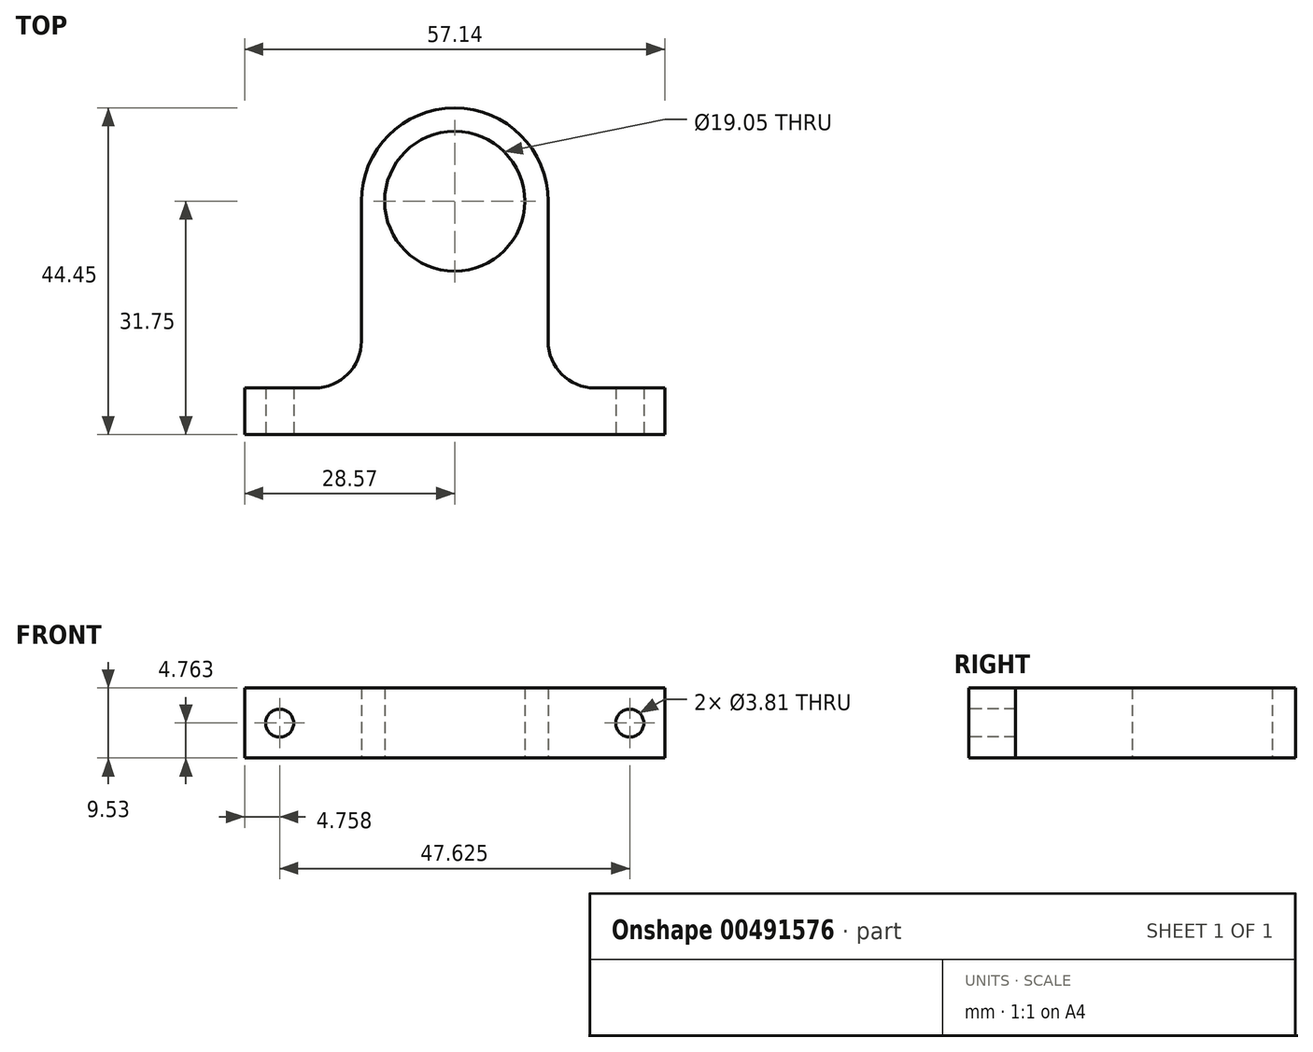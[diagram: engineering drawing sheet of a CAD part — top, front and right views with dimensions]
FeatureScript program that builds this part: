
annotation { "Feature Type Name" : "Feature", "Feature Type Description" : "" }
export const myFeature = defineFeature(function(context is Context, id is Id, definition is map)
    precondition{}
    {
        {
            var Q0;
            Q0=qCreatedBy(makeId("Top.planeOp"),FACE);
            var sketch = newSketch(context, id + "F0", { "sketchPlane" : qUnion([Q0])});
            skLineSegment(sketch, "E0", {"start": v(-28.58, -19.05) * mm, "end": v(-28.58, -12.7) * mm});
            skLineSegment(sketch, "E1", {"start": v(-28.58, -12.7) * mm, "end": v(-19.05, -12.7) * mm});
            skArc(sketch, "E2", {"start": v(-12.7, 12.7) * mm, "mid": v(-8.98, 21.68) * mm, "end": v(0, 25.4) * mm});
            skLineSegment(sketch, "E3", {"start": v(-28.58, -19.05) * mm, "end": v(0, -19.05) * mm});
            skArc(sketch, "E4.MirrorCS", {"start": v(12.7, 12.7) * mm, "mid": v(8.98, 21.68) * mm, "end": v(0, 25.4) * mm});
            skLineSegment(sketch, "E5.MirrorCS", {"start": v(28.58, -12.7) * mm, "end": v(19.05, -12.7) * mm});
            skLineSegment(sketch, "E6.MirrorCS", {"start": v(28.58, -19.05) * mm, "end": v(28.58, -12.7) * mm});
            skLineSegment(sketch, "E7.MirrorCS", {"start": v(28.58, -19.05) * mm, "end": v(0, -19.05) * mm});
            skLineSegment(sketch, "E8", {"start": v(-12.7, 12.7) * mm, "end": v(-12.7, -6.35) * mm});
            skLineSegment(sketch, "E9.MirrorCS", {"start": v(12.7, 12.7) * mm, "end": v(12.7, -6.35) * mm});
            skArc(sketch, "E10", {"start": v(-19.05, -12.7) * mm, "mid": v(-14.56, -10.84) * mm, "end": v(-12.7, -6.35) * mm});
            skArc(sketch, "E11", {"start": v(19.05, -12.7) * mm, "mid": v(14.56, -10.84) * mm, "end": v(12.7, -6.35) * mm});
            skCircle(sketch, "E12", {"center": v(0, 12.7) * mm, "radius": 9.53 * mm});
            skSolve(sketch);
        }
        {
            var Q0;
            Q0=makeQuery(id+"F0.imprint","IMPRINT",FACE,{"disambiguationData":[TD([[makeQuery(id+"F0.imprint","IMPRINT",EDGE,{"derivedFrom":sQuery(id+"F0.wireOp",EDGE,"E0")}),-1.0]])]});
            extrude(context, id + "F1", {"entities" : qUnion([Q0]), "depth" : 9.52 * mm});
        }
        {
            var Q0;
            Q0=makeQuery(id+"F1.opExtrude","SWEPT_FACE",FACE,{"disambiguationData":[OSD([sQuery(id+"F0.wireOp",EDGE,"E3"),sQuery(id+"F0.wireOp",EDGE,"E7.MirrorCS")])]});
            var sketch = newSketch(context, id + "F2", { "sketchPlane" : qUnion([Q0])});
            skPoint(sketch, "E13", {"position": v(-23.81, 4.76) * mm});
            skPoint(sketch, "E14.MirrorP", {"position": v(23.81, 4.76) * mm});
            skCircle(sketch, "E15", {"center": v(-23.81, 4.76) * mm, "radius": 1.9 * mm});
            skCircle(sketch, "E16.MirrorC", {"center": v(23.81, 4.76) * mm, "radius": 1.9 * mm});
            skSolve(sketch);
        }
        {
            var Q0;
            Q0 = qSketchRegion(id + "F2", true);
            extrude(context, id + "F3", {"entities" : qUnion([Q0]), "operationType" : NewBodyOperationType.REMOVE, "oppositeDirection" : true, "depth" : 25.4 * mm});
        }
    });
